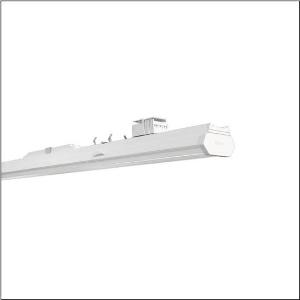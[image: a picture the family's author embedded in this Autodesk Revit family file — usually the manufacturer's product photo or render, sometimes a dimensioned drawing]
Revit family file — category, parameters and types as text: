
# Revit family: licross_r__21_protected_ho_52td11mn4fxs_06ba
name_source: partatom
category: Lighting Fixtures
units: mm (PartAtom-declared; Revit-internal decimal feet)

## family parameters
Cut with Voids When Loaded = No
Host = Face
Light Source = No
Part Type = Normal
Room Calculation Point = No
Round Connector Dimension = Use Diameter
Shared = No

## types (1)
- --- (1 x LED, 15020 lm, 83.2 W, 4000K)
    Apparent Load = 83 VA
    CIE Flux Codes = 84 94 98 99 100
    Color Rendering = 80
    Color Temperature = 4000K
    Default Elevation = 1800 mm
    Description = Licross® 21 Protected HO, luminaire insert, of sheet steel, galvanised, coil coated, white, length: 1.500mm, width: 66mm, height: 67mm, LED rated luminous flux: 15.020lm, light colour: 840, control gear: ON/OFF Multilumen, with plug, 3-pole, with phase selection, mains connection: 220..240V, AC, 50/60Hz, rated input power: 83W, halogen-free wiring, primary light control with lens, of plastic, primary optical cover: cover, of PMMA, light emission: direct distribution, primary light characteristic: symmetric, protection rating (complete): IP54, insulation class (complete): insulation class I (protective earthing), certification: CE, ENEC, VDE, UKCA, protection symbol: D if used in an environment with non-conductive dust loads with corresponding accessories, impact resistance: IK06, permissible ambient temperature for indoor applications: -35..+35°C, corresponds to IFS (International Featured Standards) requirements for safety and quality in the food industry, reducing of maximum allowable ambient temperature of 5°C with ceiling mounting, LABS conformity tested according to VDMA 24364:2018-05, packaging unit: 1 piece
    Height = 92 mm
    Lamp = 1 x LED
    Lamp Light Flux = 15020 lm
    Lamp Power = 83.2 W
    Lamp count = 1
    Length = 1500 mm
    Luminous efficacy = 181 lm/W
    Manufacturer = Siteco
    ModVariant = No
    Model = 52TD11MN4FXS
    Mounting Place = Ceiling
    Mounting Type = Pendant
    Number of Poles = 1
    OnlyDefault = Yes
    Power Factor = 1
    Product Name = Licross® 21 Protected HO
    Product group = luminaire insert
    ProductGroupID = 901
    Protection Class = Protection class I
    Protection Degree = IP 54
    RLX_Detail_Level = 1
    RLX_Emergency_Light_Flux = 0 lm
    RLX_Emergency_Type = 0
    RLX_Emergency_Type_DB = No
    RlxData = <blob elided: 21961 chars, md5=ca85f1d3>
    Socket = socket
    Standby Power = 0 W
    System Light Flux = 15020 lm
    System Power = 83 W
    Type Comments = factory setting: luminous flux: 100 % | (A | C | E) | 195 mA
    Type Image = l_1256148.jpg
    URL = http://relux.com
    VarID = @adj_039237
    Voltage = 0 V
    Weight = 0.00 kg
    Width = 88 mm

## geometry (parser evidence)
native form markers: Blend x4, Sweep x10
no freeform markers — native parametric forms only
